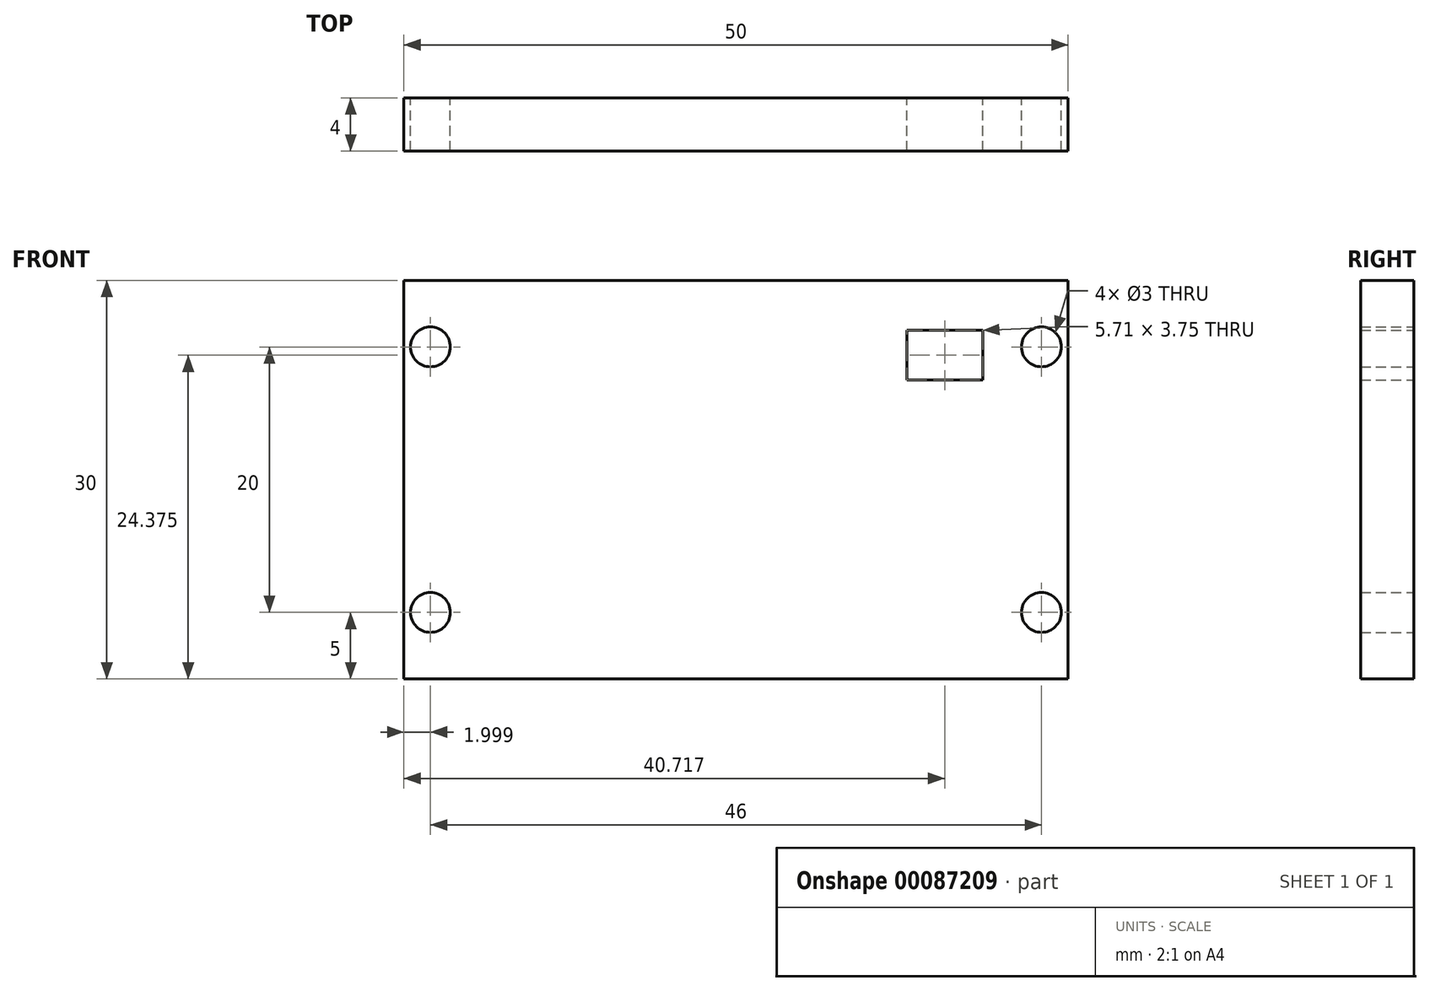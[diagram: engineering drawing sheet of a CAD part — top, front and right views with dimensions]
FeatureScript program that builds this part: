
annotation { "Feature Type Name" : "Feature", "Feature Type Description" : "" }
export const myFeature = defineFeature(function(context is Context, id is Id, definition is map)
    precondition{}
    {
        {
            var Q0;
            Q0=qCreatedBy(makeId("Front.planeOp"),FACE);
            var sketch = newSketch(context, id + "F0", { "sketchPlane" : qUnion([Q0])});
            skLineSegment(sketch, "E0.bottom", {"start": v(22.09, 0) * mm, "end": v(-27.91, 0) * mm});
            skLineSegment(sketch, "E0.top", {"start": v(22.09, 30) * mm, "end": v(-27.91, 30) * mm});
            skLineSegment(sketch, "E0.left", {"start": v(22.09, 0) * mm, "end": v(22.09, 30) * mm});
            skLineSegment(sketch, "E0.right", {"start": v(-27.91, 0) * mm, "end": v(-27.91, 30) * mm});
            skLineSegment(sketch, "E1", {"start": v(22.09, 15) * mm, "end": v(-27.91, 15) * mm});
            skLineSegment(sketch, "E2", {"start": v(9.95, 22.5) * mm, "end": v(15.66, 22.5) * mm});
            skLineSegment(sketch, "E3", {"start": v(9.95, 22.5) * mm, "end": v(9.95, 26.25) * mm});
            skLineSegment(sketch, "E4", {"start": v(22.09, 15) * mm, "end": v(22.09, 7.5) * mm});
            skLineSegment(sketch, "E5", {"start": v(9.95, 26.25) * mm, "end": v(15.66, 26.25) * mm});
            skLineSegment(sketch, "E6", {"start": v(15.66, 26.25) * mm, "end": v(15.66, 22.5) * mm});
            skCircle(sketch, "E7", {"center": v(20.09, 25) * mm, "radius": 1.5 * mm});
            skCircle(sketch, "E8", {"center": v(20.09, 5) * mm, "radius": 1.5 * mm});
            skLineSegment(sketch, "E9.bottom", {"start": v(-27.91, 0) * mm, "end": v(-25.91, 0) * mm});
            skLineSegment(sketch, "E9.left", {"start": v(-27.91, 0) * mm, "end": v(-27.91, 5) * mm});
            skCircle(sketch, "E10", {"center": v(-25.91, 5) * mm, "radius": 1.5 * mm});
            skLineSegment(sketch, "E11.bottom", {"start": v(-27.91, 30) * mm, "end": v(-25.91, 30) * mm});
            skLineSegment(sketch, "E11.left", {"start": v(-27.91, 30) * mm, "end": v(-27.91, 25) * mm});
            skCircle(sketch, "E12", {"center": v(-25.91, 25) * mm, "radius": 1.5 * mm});
            skPoint(sketch, "E13.trimOffspring.end.orphan", {"position": v(0, 0) * mm});
            skSolve(sketch);
        }
        {
            var Q0;
            Q0 = qSketchRegion(id + "F0", true);
            extrude(context, id + "F1", {"entities" : qUnion([Q0]), "depth" : 4 * mm});
        }
    });
